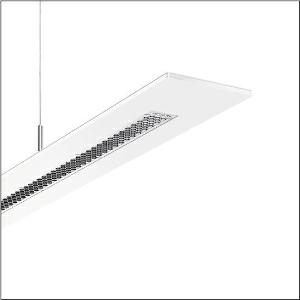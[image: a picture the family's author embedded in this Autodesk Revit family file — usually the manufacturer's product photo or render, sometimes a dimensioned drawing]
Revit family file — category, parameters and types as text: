
# Revit family: arktika_r__21_5mb2512l30830_74ae
name_source: partatom
category: Lighting Fixtures
units: mm (PartAtom-declared; Revit-internal decimal feet)

## family parameters
Cut with Voids When Loaded = No
Host = Face
Light Source = No
Part Type = Normal
Room Calculation Point = No
Round Connector Dimension = Use Diameter
Shared = No

## types (1)
- Arktika® 21 (1 x LED 3000K / CRI = 80 (unbekannt), 3670 lm, 3000K)
    Apparent Load = 31 VA
    CIE Flux Codes = 81 100 100 79 100
    Color Rendering = 80
    Color Temperature = 3000K
    Default Elevation = 1800 mm
    Description = Arktika® 21, office luminaire, primary anti-glare with honeycomb louvre, of plastic, aluminium vaporised, highly specular, light emission: direct/indirect distribution, primary light characteristic: symmetric, installation type: suspended mounting, LED, rated luminous flux: 3.670lm, luminous efficacy: 120lm/W, light colour: 830, colour temperature: 3000K, control gear: ECG, with terminal, 3-pole, mains connection: 220..240V, AC, 50/60Hz, rated input power: 31W, housing, of aluminium, powder-coated, traffic white (RAL 9016), 1-length, length: 1.250mm, width: 120mm, height: 8mm, protection rating (complete): IP20, insulation class (complete): insulation class II (safety insulation), certification: CE, packaging unit: 1 piece
    Height = 8 mm  [stored 0.0262467 ft]
    Lamp = 1 x LED 3000K / CRI >= 80 (unbekannt)
    Lamp Light Flux = 3670 lm
    Lamp count = 1
    Length = 1250 mm
    Luminous efficacy = 120 lm/W
    Manufacturer = Siteco
    ModVariant = No
    Model = 5MB2512L30830
    Mounting Place = Ceiling
    Mounting Type = Pendant
    Number of Poles = 1
    OnlyDefault = Yes
    Power Factor = 1
    Product Name = Arktika® 21
    Product group = office luminaire | ceiling pendant
    ProductGroupID = 902
    Protection Class = Protection class II
    Protection Degree = IP 20
    RLX_Detail_Level = 1
    RLX_Emergency_Light_Flux = 0 lm
    RLX_Emergency_Type = 0
    RLX_Emergency_Type_DB = No
    RlxData = <blob elided: 36013 chars, md5=dcea7be3>
    Socket = socket
    Standby Power = 0 W
    System Light Flux = 3670 lm
    System Power = 31 W
    Type Comments = Product without accessories
    Type Image = l_1006128.jpg
    URL = http://relux.com
    VarID = ---
    Voltage = 0 V
    Weight = 0.00 kg
    Width = 120 mm

note: [stored X ft] marks values corroborated as IEEE doubles in the binary element streams (Revit-internal decimal feet)

## geometry (parser evidence)
native form markers: Blend x4, Sweep x12
no freeform markers — native parametric forms only
